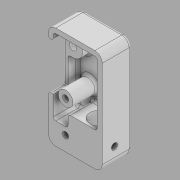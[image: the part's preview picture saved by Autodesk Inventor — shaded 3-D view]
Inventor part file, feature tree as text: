
AUTODESK INVENTOR PART (.ipt)
format: ipt  version: 2020 (Build 240168000, 168)  size: 396,288 bytes
history: native  units: in
note: dims shown in document units (in); Inventor stores cm internally (conversion verified against a paired STEP export)
features: sketch x10, projected_geometry x8, extrude x5, hole x5, fillet x4
ambient origin geometry x8: Origin, YZ Plane, XZ Plane, XY Plane, X Axis, Y Axis, Z Axis, Center Point
bodies: Solid1 (feature_tree)
feature tree (32):
  extrude  "Extrusion1"  Depth=2.75in
  extrude  "Extrusion2"  Depth=1.5in TaperAngle=0.0deg
  extrude  "Extrusion3"  Depth=0.25in
  extrude  "Extrusion4"  Depth=1.5in
  extrude  "Extrusion5"  Depth=1.25in TaperAngle=0.0deg
  hole  "Hole1"  [1 undecoded]
  fillet  "Fillet1"  Radius=0.625in
  fillet  "Fillet2"  Radius=0.125in
  fillet  "Fillet3"  Radius=0.25in
  fillet  "Fillet4"  Radius=1.0in
  hole  "Hole2"  [1 undecoded]
  hole  "Hole6"  [1 undecoded]
  hole  "Hole7"  [1 undecoded]
  hole  "Hole8"  [1 undecoded]
  sketch  "Sketch1"  dims[d0=5.25in d1=2.75in]
  sketch  "Sketch2"  dims[d2=0.375in d3=1.5in d4=0.0in]
  projected_geometry  "Projected Loop1"
  sketch  "Sketch3"  dims[d5=0.25in d6=0.25in]
  projected_geometry  "Projected Loop2"
  sketch  "Sketch4"  dims[d7=1.5in d8=0.625in]
  projected_geometry  "Projected Loop3"
  projected_geometry  "Projected Loop4"
  projected_geometry  "Projected Loop5"
  sketch  "Sketch5"  dims[d9=1.75in d10=1.25in d11=0.0in]
  projected_geometry  "Projected Loop6"
  projected_geometry  "Projected Loop7"
  sketch  "Sketch6"  dims[d12=0.75in d13=2.375in d14=0.625in d15=0.125in d16=0.25in d17=0.0in d18=1.0in]
  sketch  "Sketch7"  dims[d19=4.125in d20=0.5in]
  projected_geometry  "Projected Loop8"
  sketch  "Sketch11"  dims[d23=0.5in d24=0.0in d25=0.75in]
  sketch  "Sketch12"  dims[d26=2.375in d27=0.875in]
  sketch  "Sketch13"  dims[d28=1.25in d29=0.0in d30=0.75in d31=0.625in d32=1.0in d33=0.276in d34=0.375in d35=0.25in d36=0.5635in d37=0.181in d38=0.8108in d39=0.125in d40=0.125in d41=0.125in d42=0.125in d43=0.375in d44=0.276in d45=0.375in d46=0.25in d47=0.5635in d48=0.181in d49=0.8108in d75=0.625in d76=0.875in d77=0.3125in d78=0.75in d79=0.75in d80=0.188in d81=0.5635in d82=0.6in d83=0.0in d86=0.875in d87=2.375in d88=0.3125in d89=0.75in d90=0.5in d91=0.3125in d92=0.5635in d93=0.6in d94=0.0in d95=0.875in d96=0.75in d97=0.3125in d98=0.75in d99=0.5in d100=0.3125in d101=0.5635in d102=0.6in d103=0.0in]
note: 5 required parameter values undecoded (feature->parameter linkage not recoverable at this tier; creation-order binding heuristic only, values carry confidence <= 0.55)
